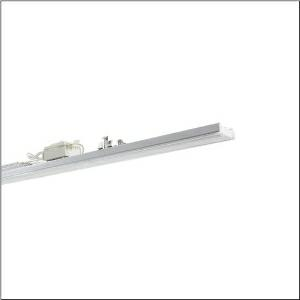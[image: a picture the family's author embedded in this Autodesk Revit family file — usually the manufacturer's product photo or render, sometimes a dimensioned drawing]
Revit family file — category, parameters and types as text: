
# Revit family: licross_11_recessed_mo_51tl187n485g
name_source: partatom
category: Lighting Fixtures
units: mm (PartAtom-declared; Revit-internal decimal feet)

## family parameters
Cut with Voids When Loaded = No
Host = Face
Light Source = No
Part Type = Normal
Room Calculation Point = No
Round Connector Dimension = Use Diameter
Shared = No

## types (1)
- Licross 11 Recessed MO (1 x LED, 8700 lm, 48.5 W, 4000K)
    Apparent Load = 49 VA
    CIE Flux Codes = 83 96 99 100 100
    Color Rendering = 80
    Color Temperature = 4000K
    Default Elevation = 1800 mm
    Description = Licross 11 Recessed MO, luminaire insert, of sheet steel, coil coated, white, length: 1.500mm, width: 66mm, height: 67mm, LED rated luminous flux: 8.700lm, light colour: 840, SDCM (Standard Deviation of Colour Matching)MacAdam ≤ 2 SDCM (initial), control gear: ON/OFF, with plug, 3-pole, with phase selection, mains connection: 220..240V, AC, 50/60Hz, rated input power: 49W, internal wiring halogen-free, primary light control with lens, of plastic, primary optical cover: cover, of PMMA, light emission: direct distribution, primary light characteristic: symmetric, protection rating (complete): IP40, insulation class (complete): insulation class I (protective earthing), certification: CE, ENEC, VDE, UKCA, protection symbol: D if used in an environment without relevant dust loads with corresponding accessories, impact resistance: IK06, permissible ambient temperature for indoor applications: -35..+35°C, corresponds to IFS (International Featured Standards) requirements for safety and quality in the food industry, reducing of maximum allowable ambient temperature of 5°C with ceiling mounting, The light source and the operating device comply with the requirements of the Ecodesign Regulation (EU) 2019/2020 and are replaceable in accordance with this regulation, packaging unit: 1 piece
    Height = 58 mm
    Lamp = 1 x LED
    Lamp Light Flux = 8700 lm
    Lamp Power = 48.5 W
    Lamp count = 1
    Length = 1500 mm
    Luminous efficacy = 179 lm/W
    Manufacturer = Siteco
    ModVariant = No
    Model = 51TL187N485G
    Mounting Place = Ceiling
    Mounting Type = Pendant
    Number of Poles = 1
    OnlyDefault = Yes
    Power Factor = 1
    Product Name = Licross 11 Recessed MO
    Product group = luminaire insert | ceiling pendant
    ProductGroupID = 901
    Protection Class = Protection class I
    Protection Degree = IP 40
    RLX_Detail_Level = 1
    RLX_Emergency_Light_Flux = 0 lm
    RLX_Emergency_Type = 0
    RLX_Emergency_Type_DB = No
    RlxData = <blob elided: 21033 chars, md5=c67356ba>
    Socket = socket
    Standby Power = 0 W
    System Light Flux = 8700 lm
    System Power = 49 W
    Type Comments = Product without accessories
    Type Image = l_1296930.jpg
    URL = http://relux.com
    VarID = ---
    Voltage = 0 V
    Weight = 0.00 kg
    Width = 66 mm

## geometry (parser evidence)
native form markers: Blend x4, Sweep x12
no freeform markers — native parametric forms only
